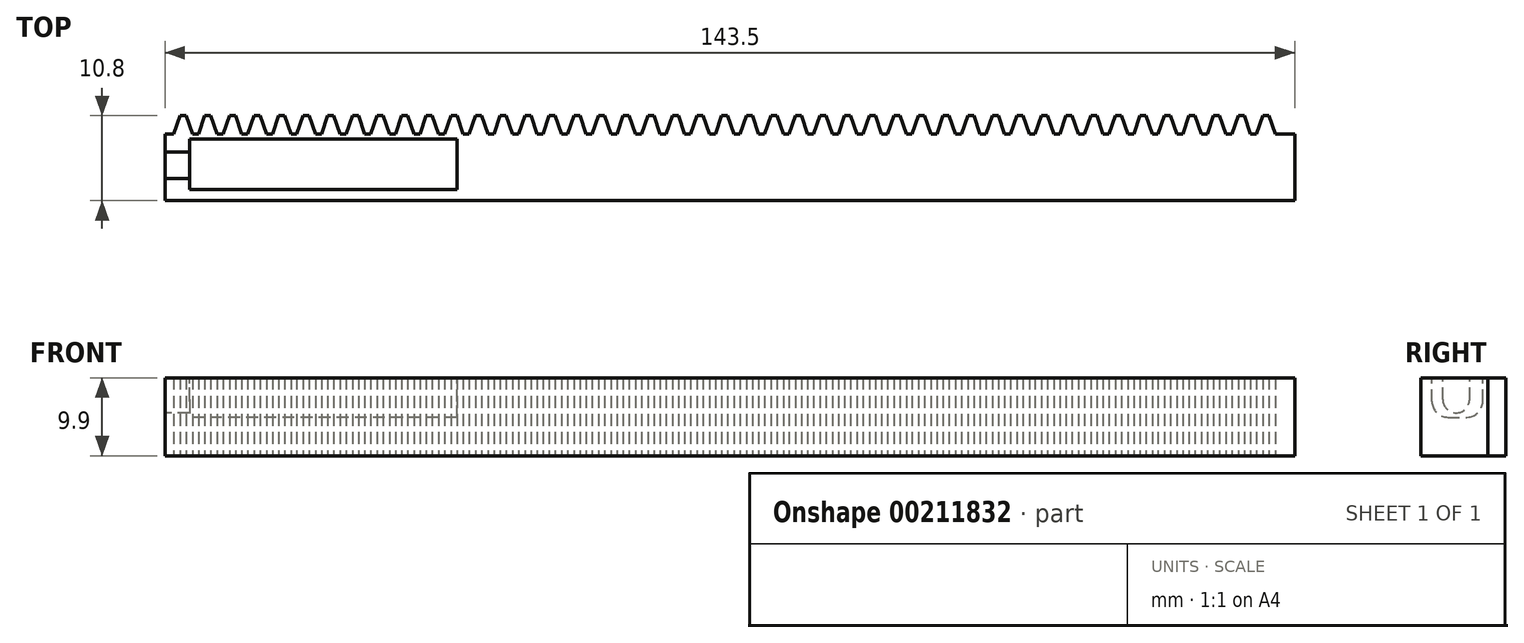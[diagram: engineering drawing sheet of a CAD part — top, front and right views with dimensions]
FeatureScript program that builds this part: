
annotation { "Feature Type Name" : "Feature", "Feature Type Description" : "" }
export const myFeature = defineFeature(function(context is Context, id is Id, definition is map)
    precondition{}
    {
        {
            var Q0;
            Q0=qCreatedBy(makeId("Top.planeOp"),FACE);
            var sketch = newSketch(context, id + "F0", { "sketchPlane" : qUnion([Q0])});
            skLineSegment(sketch, "E0.bottom", {"start": v(0, 0) * mm, "end": v(143.5, 0) * mm});
            skLineSegment(sketch, "E0.top", {"start": v(0, -8.5) * mm, "end": v(143.5, -8.5) * mm});
            skLineSegment(sketch, "E0.left", {"start": v(0, 0) * mm, "end": v(0, -8.5) * mm});
            skLineSegment(sketch, "E0.right", {"start": v(143.5, 0) * mm, "end": v(143.5, -8.5) * mm});
            skLineSegment(sketch, "E1", {"start": v(1.9, 2.3) * mm, "end": v(2.67, 2.3) * mm});
            skLineSegment(sketch, "E2", {"start": v(2.67, 2.3) * mm, "end": v(3.47, 0) * mm});
            skLineSegment(sketch, "E3", {"start": v(3.47, 0) * mm, "end": v(4.23, 0) * mm});
            skLineSegment(sketch, "E4", {"start": v(4.23, 0) * mm, "end": v(5.04, 2.3) * mm});
            skLineSegment(sketch, "E5", {"start": v(5.04, 2.3) * mm, "end": v(5.8, 2.3) * mm});
            skLineSegment(sketch, "E6", {"start": v(5.8, 2.3) * mm, "end": v(6.6, 0) * mm});
            skLineSegment(sketch, "E7", {"start": v(6.6, 0) * mm, "end": v(7.36, 0) * mm});
            skLineSegment(sketch, "E8", {"start": v(7.36, 0) * mm, "end": v(8.17, 2.3) * mm});
            skLineSegment(sketch, "E9", {"start": v(8.17, 2.3) * mm, "end": v(8.93, 2.3) * mm});
            skLineSegment(sketch, "E10", {"start": v(8.93, 2.3) * mm, "end": v(9.73, 0) * mm});
            skLineSegment(sketch, "E11", {"start": v(9.73, 0) * mm, "end": v(16.36, 0) * mm});
            skLineSegment(sketch, "E12", {"start": v(1.9, 2.3) * mm, "end": v(1.1, 0) * mm});
            skLineSegment(sketch, "E13", {"start": v(2.28, 2.3) * mm, "end": v(2.28, 0) * mm});
            skLineSegment(sketch, "E14", {"start": v(9.73, 0) * mm, "end": v(10.5, 0) * mm});
            skLineSegment(sketch, "E15", {"start": v(10.5, 0) * mm, "end": v(11.3, 2.3) * mm});
            skLineSegment(sketch, "E16", {"start": v(11.3, 2.3) * mm, "end": v(12.06, 2.3) * mm});
            skLineSegment(sketch, "E17", {"start": v(12.06, 2.3) * mm, "end": v(12.86, 0) * mm});
            skLineSegment(sketch, "E18", {"start": v(12.86, 0) * mm, "end": v(13.62, 0) * mm});
            skLineSegment(sketch, "E19", {"start": v(13.62, 0) * mm, "end": v(14.43, 2.3) * mm});
            skLineSegment(sketch, "E20", {"start": v(14.43, 2.3) * mm, "end": v(15.19, 2.3) * mm});
            skLineSegment(sketch, "E21", {"start": v(15.19, 2.3) * mm, "end": v(16, 0) * mm});
            skLineSegment(sketch, "E22", {"start": v(13.62, 0) * mm, "end": v(12.86, 0) * mm});
            skLineSegment(sketch, "E23", {"start": v(10.5, 0) * mm, "end": v(9.73, 0) * mm});
            skPoint(sketch, "E24", {"position": v(0.73, 0) * mm});
            skPoint(sketch, "E25", {"position": v(32, 0) * mm});
            skPoint(sketch, "E26", {"position": v(47.62, 0) * mm});
            skPoint(sketch, "E27", {"position": v(63.25, 0) * mm});
            skPoint(sketch, "E28", {"position": v(78.88, 0) * mm});
            skPoint(sketch, "E29", {"position": v(94.51, 0) * mm});
            skPoint(sketch, "E30", {"position": v(110.14, 0) * mm});
            skPoint(sketch, "E31", {"position": v(125.76, 0) * mm});
            skPoint(sketch, "E32", {"position": v(141.4, 0) * mm});
            skLineSegment(sketch, "E33", {"start": v(16.36, 0) * mm, "end": v(16.36, -2.94) * mm});
            skLineSegment(sketch, "E34", {"start": v(32, 0) * mm, "end": v(32, -2.44) * mm});
            skLineSegment(sketch, "E35", {"start": v(47.62, 0) * mm, "end": v(47.62, -3.03) * mm});
            skLineSegment(sketch, "E36", {"start": v(63.25, 0) * mm, "end": v(63.25, -3.22) * mm});
            skLineSegment(sketch, "E37", {"start": v(78.88, 0) * mm, "end": v(78.88, -3.55) * mm});
            skLineSegment(sketch, "E38", {"start": v(94.51, 0) * mm, "end": v(94.51, -3.55) * mm});
            skLineSegment(sketch, "E39", {"start": v(110.14, 0) * mm, "end": v(110.14, -2.9) * mm});
            skLineSegment(sketch, "E40", {"start": v(125.76, 0) * mm, "end": v(125.76, -2.77) * mm});
            skLineSegment(sketch, "E41.MirrorCS", {"start": v(22.23, 0) * mm, "end": v(23, 0) * mm});
            skLineSegment(sketch, "E42.MirrorCS", {"start": v(26.12, 0) * mm, "end": v(25.36, 0) * mm});
            skLineSegment(sketch, "E43.MirrorCS", {"start": v(23, 0) * mm, "end": v(16.36, 0) * mm});
            skLineSegment(sketch, "E44.MirrorCS", {"start": v(23, 0) * mm, "end": v(22.23, 0) * mm});
            skLineSegment(sketch, "E45.MirrorCS", {"start": v(30.82, 2.3) * mm, "end": v(30.06, 2.3) * mm});
            skLineSegment(sketch, "E46.MirrorCS", {"start": v(19.86, 0) * mm, "end": v(19.1, 0) * mm});
            skLineSegment(sketch, "E47.MirrorCS", {"start": v(21.43, 2.3) * mm, "end": v(20.67, 2.3) * mm});
            skLineSegment(sketch, "E48.MirrorCS", {"start": v(22.23, 0) * mm, "end": v(21.43, 2.3) * mm});
            skLineSegment(sketch, "E49.MirrorCS", {"start": v(32.72, 0) * mm, "end": v(-110.78, 0) * mm});
            skLineSegment(sketch, "E50.MirrorCS", {"start": v(26.93, 2.3) * mm, "end": v(26.12, 0) * mm});
            skLineSegment(sketch, "E51.MirrorCS", {"start": v(23.8, 2.3) * mm, "end": v(23, 0) * mm});
            skLineSegment(sketch, "E52.MirrorCS", {"start": v(19.1, 0) * mm, "end": v(19.86, 0) * mm});
            skLineSegment(sketch, "E53.MirrorCS", {"start": v(27.69, 2.3) * mm, "end": v(26.93, 2.3) * mm});
            skLineSegment(sketch, "E54.MirrorCS", {"start": v(24.56, 2.3) * mm, "end": v(23.8, 2.3) * mm});
            skLineSegment(sketch, "E55.MirrorCS", {"start": v(18.3, 2.3) * mm, "end": v(17.53, 2.3) * mm});
            skLineSegment(sketch, "E56.MirrorCS", {"start": v(19.1, 0) * mm, "end": v(18.3, 2.3) * mm});
            skLineSegment(sketch, "E57.MirrorCS", {"start": v(20.67, 2.3) * mm, "end": v(19.86, 0) * mm});
            skLineSegment(sketch, "E58.MirrorCS", {"start": v(25.36, 0) * mm, "end": v(24.56, 2.3) * mm});
            skLineSegment(sketch, "E59.MirrorCS", {"start": v(28.5, 0) * mm, "end": v(27.69, 2.3) * mm});
            skLineSegment(sketch, "E60.MirrorCS", {"start": v(30.82, 2.3) * mm, "end": v(31.62, 0) * mm});
            skLineSegment(sketch, "E61.MirrorCS", {"start": v(30.06, 2.3) * mm, "end": v(29.25, 0) * mm});
            skLineSegment(sketch, "E62.MirrorCS", {"start": v(29.25, 0) * mm, "end": v(28.5, 0) * mm});
            skLineSegment(sketch, "E63.MirrorCS", {"start": v(17.53, 2.3) * mm, "end": v(16.73, 0) * mm});
            skLineSegment(sketch, "E64.MirrorCS", {"start": v(30.44, 2.3) * mm, "end": v(30.44, 0) * mm});
            skLineSegment(sketch, "E65.MirrorCS", {"start": v(53.5, 0) * mm, "end": v(54.25, 0) * mm});
            skLineSegment(sketch, "E66.MirrorCS", {"start": v(41.75, 0) * mm, "end": v(41, 0) * mm});
            skLineSegment(sketch, "E67.MirrorCS", {"start": v(41, 0) * mm, "end": v(41.75, 0) * mm});
            skLineSegment(sketch, "E68.MirrorCS", {"start": v(54.25, 0) * mm, "end": v(53.5, 0) * mm});
            skLineSegment(sketch, "E69.MirrorCS", {"start": v(51.12, 0) * mm, "end": v(50.36, 0) * mm});
            skLineSegment(sketch, "E70.MirrorCS", {"start": v(44.88, 0) * mm, "end": v(44.12, 0) * mm});
            skLineSegment(sketch, "E71.MirrorCS", {"start": v(50.36, 0) * mm, "end": v(51.12, 0) * mm});
            skLineSegment(sketch, "E72.MirrorCS", {"start": v(44.12, 0) * mm, "end": v(44.88, 0) * mm});
            skLineSegment(sketch, "E73.MirrorCS", {"start": v(47.62, 0) * mm, "end": v(47.62, -2.94) * mm});
            skLineSegment(sketch, "E74.MirrorCS", {"start": v(45.69, 2.3) * mm, "end": v(46.45, 2.3) * mm});
            skLineSegment(sketch, "E75.MirrorCS", {"start": v(39.43, 2.3) * mm, "end": v(40.19, 2.3) * mm});
            skLineSegment(sketch, "E76.MirrorCS", {"start": v(33.17, 2.3) * mm, "end": v(33.93, 2.3) * mm});
            skLineSegment(sketch, "E77.MirrorCS", {"start": v(36.3, 2.3) * mm, "end": v(37.06, 2.3) * mm});
            skLineSegment(sketch, "E78.MirrorCS", {"start": v(49.55, 2.3) * mm, "end": v(48.8, 2.3) * mm});
            skLineSegment(sketch, "E79.MirrorCS", {"start": v(55.82, 2.3) * mm, "end": v(55.06, 2.3) * mm});
            skLineSegment(sketch, "E80.MirrorCS", {"start": v(57.38, 0) * mm, "end": v(56.62, 0) * mm});
            skLineSegment(sketch, "E81.MirrorCS", {"start": v(58.95, 2.3) * mm, "end": v(58.19, 2.3) * mm});
            skLineSegment(sketch, "E82.MirrorCS", {"start": v(60.51, 0) * mm, "end": v(59.75, 0) * mm});
            skLineSegment(sketch, "E83.MirrorCS", {"start": v(42.56, 2.3) * mm, "end": v(43.32, 2.3) * mm});
            skLineSegment(sketch, "E84.MirrorCS", {"start": v(37.86, 0) * mm, "end": v(38.62, 0) * mm});
            skLineSegment(sketch, "E85.MirrorCS", {"start": v(62.08, 2.3) * mm, "end": v(61.32, 2.3) * mm});
            skLineSegment(sketch, "E86.MirrorCS", {"start": v(52.69, 2.3) * mm, "end": v(51.93, 2.3) * mm});
            skLineSegment(sketch, "E87.MirrorCS", {"start": v(34.73, 0) * mm, "end": v(35.5, 0) * mm});
            skLineSegment(sketch, "E88.MirrorCS", {"start": v(54.25, 0) * mm, "end": v(47.62, 0) * mm});
            skLineSegment(sketch, "E89.MirrorCS", {"start": v(41, 0) * mm, "end": v(47.62, 0) * mm});
            skLineSegment(sketch, "E90.MirrorCS", {"start": v(31.26, 0) * mm, "end": v(174.76, 0) * mm});
            skLineSegment(sketch, "E91.MirrorCS", {"start": v(53.5, 0) * mm, "end": v(52.69, 2.3) * mm});
            skLineSegment(sketch, "E92.MirrorCS", {"start": v(48.8, 2.3) * mm, "end": v(47.99, 0) * mm});
            skLineSegment(sketch, "E93.MirrorCS", {"start": v(33.93, 2.3) * mm, "end": v(34.73, 0) * mm});
            skLineSegment(sketch, "E94.MirrorCS", {"start": v(61.7, 2.3) * mm, "end": v(61.7, 0) * mm});
            skLineSegment(sketch, "E95.MirrorCS", {"start": v(33.17, 2.3) * mm, "end": v(32.36, 0) * mm});
            skLineSegment(sketch, "E96.MirrorCS", {"start": v(56.62, 0) * mm, "end": v(55.82, 2.3) * mm});
            skLineSegment(sketch, "E97.MirrorCS", {"start": v(58.19, 2.3) * mm, "end": v(57.38, 0) * mm});
            skLineSegment(sketch, "E98.MirrorCS", {"start": v(59.75, 0) * mm, "end": v(58.95, 2.3) * mm});
            skLineSegment(sketch, "E99.MirrorCS", {"start": v(33.55, 2.3) * mm, "end": v(33.55, 0) * mm});
            skLineSegment(sketch, "E100.MirrorCS", {"start": v(40.19, 2.3) * mm, "end": v(41, 0) * mm});
            skLineSegment(sketch, "E101.MirrorCS", {"start": v(38.62, 0) * mm, "end": v(39.43, 2.3) * mm});
            skLineSegment(sketch, "E102.MirrorCS", {"start": v(37.06, 2.3) * mm, "end": v(37.86, 0) * mm});
            skLineSegment(sketch, "E103.MirrorCS", {"start": v(43.32, 2.3) * mm, "end": v(44.12, 0) * mm});
            skLineSegment(sketch, "E104.MirrorCS", {"start": v(51.93, 2.3) * mm, "end": v(51.12, 0) * mm});
            skLineSegment(sketch, "E105.MirrorCS", {"start": v(62.08, 2.3) * mm, "end": v(62.88, 0) * mm});
            skLineSegment(sketch, "E106.MirrorCS", {"start": v(41.75, 0) * mm, "end": v(42.56, 2.3) * mm});
            skLineSegment(sketch, "E107.MirrorCS", {"start": v(46.45, 2.3) * mm, "end": v(47.25, 0) * mm});
            skLineSegment(sketch, "E108.MirrorCS", {"start": v(61.32, 2.3) * mm, "end": v(60.51, 0) * mm});
            skLineSegment(sketch, "E109.MirrorCS", {"start": v(35.5, 0) * mm, "end": v(36.3, 2.3) * mm});
            skLineSegment(sketch, "E110.MirrorCS", {"start": v(55.06, 2.3) * mm, "end": v(54.25, 0) * mm});
            skLineSegment(sketch, "E111.MirrorCS", {"start": v(44.88, 0) * mm, "end": v(45.69, 2.3) * mm});
            skLineSegment(sketch, "E112.MirrorCS", {"start": v(50.36, 0) * mm, "end": v(49.55, 2.3) * mm});
            skLineSegment(sketch, "E113.MirrorCS", {"start": v(63.98, 0) * mm, "end": v(-79.52, 0) * mm});
            skLineSegment(sketch, "E114.MirrorCS", {"start": v(84.75, 0) * mm, "end": v(85.51, 0) * mm});
            skLineSegment(sketch, "E115.MirrorCS", {"start": v(116.01, 0) * mm, "end": v(116.77, 0) * mm});
            skLineSegment(sketch, "E116.MirrorCS", {"start": v(73.01, 0) * mm, "end": v(72.25, 0) * mm});
            skLineSegment(sketch, "E117.MirrorCS", {"start": v(104.27, 0) * mm, "end": v(103.51, 0) * mm});
            skLineSegment(sketch, "E118.MirrorCS", {"start": v(78.88, 0) * mm, "end": v(78.88, -3.03) * mm});
            skLineSegment(sketch, "E119.MirrorCS", {"start": v(85.51, 0) * mm, "end": v(84.75, 0) * mm});
            skLineSegment(sketch, "E120.MirrorCS", {"start": v(72.25, 0) * mm, "end": v(73.01, 0) * mm});
            skLineSegment(sketch, "E121.MirrorCS", {"start": v(78.88, 0) * mm, "end": v(78.88, -2.94) * mm});
            skLineSegment(sketch, "E122.MirrorCS", {"start": v(103.51, 0) * mm, "end": v(104.27, 0) * mm});
            skLineSegment(sketch, "E123.MirrorCS", {"start": v(116.77, 0) * mm, "end": v(116.01, 0) * mm});
            skLineSegment(sketch, "E124.MirrorCS", {"start": v(94.51, 0) * mm, "end": v(94.51, -2.44) * mm});
            skLineSegment(sketch, "E125.MirrorCS", {"start": v(75.38, 0) * mm, "end": v(76.14, 0) * mm});
            skLineSegment(sketch, "E126.MirrorCS", {"start": v(81.62, 0) * mm, "end": v(82.38, 0) * mm});
            skLineSegment(sketch, "E127.MirrorCS", {"start": v(107.4, 0) * mm, "end": v(106.64, 0) * mm});
            skLineSegment(sketch, "E128.MirrorCS", {"start": v(113.64, 0) * mm, "end": v(112.88, 0) * mm});
            skLineSegment(sketch, "E129.MirrorCS", {"start": v(112.88, 0) * mm, "end": v(113.64, 0) * mm});
            skLineSegment(sketch, "E130.MirrorCS", {"start": v(106.64, 0) * mm, "end": v(107.4, 0) * mm});
            skLineSegment(sketch, "E131.MirrorCS", {"start": v(123.03, 0) * mm, "end": v(122.27, 0) * mm});
            skLineSegment(sketch, "E132.MirrorCS", {"start": v(76.14, 0) * mm, "end": v(75.38, 0) * mm});
            skLineSegment(sketch, "E133.MirrorCS", {"start": v(110.14, 0) * mm, "end": v(110.14, -2.94) * mm});
            skLineSegment(sketch, "E134.MirrorCS", {"start": v(82.38, 0) * mm, "end": v(81.62, 0) * mm});
            skLineSegment(sketch, "E135.MirrorCS", {"start": v(108.2, 2.3) * mm, "end": v(108.97, 2.3) * mm});
            skLineSegment(sketch, "E136.MirrorCS", {"start": v(88.64, 0) * mm, "end": v(87.88, 0) * mm});
            skLineSegment(sketch, "E137.MirrorCS", {"start": v(87.08, 2.3) * mm, "end": v(86.32, 2.3) * mm});
            skLineSegment(sketch, "E138.MirrorCS", {"start": v(101.95, 2.3) * mm, "end": v(102.7, 2.3) * mm});
            skLineSegment(sketch, "E139.MirrorCS", {"start": v(83.95, 2.3) * mm, "end": v(83.19, 2.3) * mm});
            skLineSegment(sketch, "E140.MirrorCS", {"start": v(80.81, 2.3) * mm, "end": v(80.05, 2.3) * mm});
            skLineSegment(sketch, "E141.MirrorCS", {"start": v(95.69, 2.3) * mm, "end": v(96.45, 2.3) * mm});
            skLineSegment(sketch, "E142.MirrorCS", {"start": v(98.82, 2.3) * mm, "end": v(99.58, 2.3) * mm});
            skLineSegment(sketch, "E143.MirrorCS", {"start": v(66, 0) * mm, "end": v(66.75, 0) * mm});
            skLineSegment(sketch, "E144.MirrorCS", {"start": v(112.07, 2.3) * mm, "end": v(111.31, 2.3) * mm});
            skLineSegment(sketch, "E145.MirrorCS", {"start": v(118.34, 2.3) * mm, "end": v(117.58, 2.3) * mm});
            skLineSegment(sketch, "E146.MirrorCS", {"start": v(119.9, 0) * mm, "end": v(119.14, 0) * mm});
            skLineSegment(sketch, "E147.MirrorCS", {"start": v(121.47, 2.3) * mm, "end": v(120.7, 2.3) * mm});
            skLineSegment(sketch, "E148.MirrorCS", {"start": v(124.6, 2.3) * mm, "end": v(123.84, 2.3) * mm});
            skLineSegment(sketch, "E149.MirrorCS", {"start": v(97.25, 0) * mm, "end": v(98.01, 0) * mm});
            skLineSegment(sketch, "E150.MirrorCS", {"start": v(105.08, 2.3) * mm, "end": v(105.84, 2.3) * mm});
            skLineSegment(sketch, "E151.MirrorCS", {"start": v(93.34, 2.3) * mm, "end": v(92.58, 2.3) * mm});
            skLineSegment(sketch, "E152.MirrorCS", {"start": v(115.2, 2.3) * mm, "end": v(114.45, 2.3) * mm});
            skLineSegment(sketch, "E153.MirrorCS", {"start": v(64.43, 2.3) * mm, "end": v(65.19, 2.3) * mm});
            skLineSegment(sketch, "E154.MirrorCS", {"start": v(90.2, 2.3) * mm, "end": v(89.45, 2.3) * mm});
            skLineSegment(sketch, "E155.MirrorCS", {"start": v(70.69, 2.3) * mm, "end": v(71.45, 2.3) * mm});
            skLineSegment(sketch, "E156.MirrorCS", {"start": v(73.82, 2.3) * mm, "end": v(74.58, 2.3) * mm});
            skLineSegment(sketch, "E157.MirrorCS", {"start": v(69.12, 0) * mm, "end": v(69.88, 0) * mm});
            skLineSegment(sketch, "E158.MirrorCS", {"start": v(91.77, 0) * mm, "end": v(91.01, 0) * mm});
            skLineSegment(sketch, "E159.MirrorCS", {"start": v(93.78, 0) * mm, "end": v(237.28, 0) * mm});
            skLineSegment(sketch, "E160.MirrorCS", {"start": v(76.95, 2.3) * mm, "end": v(77.7, 2.3) * mm});
            skLineSegment(sketch, "E161.MirrorCS", {"start": v(67.56, 2.3) * mm, "end": v(68.32, 2.3) * mm});
            skLineSegment(sketch, "E162.MirrorCS", {"start": v(72.25, 0) * mm, "end": v(78.88, 0) * mm});
            skLineSegment(sketch, "E163.MirrorCS", {"start": v(100.38, 0) * mm, "end": v(101.14, 0) * mm});
            skLineSegment(sketch, "E164.MirrorCS", {"start": v(103.51, 0) * mm, "end": v(110.14, 0) * mm});
            skPoint(sketch, "E165.MirrorP", {"position": v(125.77, 0) * mm});
            skLineSegment(sketch, "E166.MirrorCS", {"start": v(85.51, 0) * mm, "end": v(78.88, 0) * mm});
            skLineSegment(sketch, "E167.MirrorCS", {"start": v(122.27, 0) * mm, "end": v(121.47, 2.3) * mm});
            skLineSegment(sketch, "E168.MirrorCS", {"start": v(123.84, 2.3) * mm, "end": v(123.03, 0) * mm});
            skLineSegment(sketch, "E169.MirrorCS", {"start": v(116.77, 0) * mm, "end": v(110.14, 0) * mm});
            skLineSegment(sketch, "E170.MirrorCS", {"start": v(62.52, 0) * mm, "end": v(206.02, 0) * mm});
            skLineSegment(sketch, "E171.MirrorCS", {"start": v(86.32, 2.3) * mm, "end": v(85.51, 0) * mm});
            skLineSegment(sketch, "E172.MirrorCS", {"start": v(116.01, 0) * mm, "end": v(115.2, 2.3) * mm});
            skLineSegment(sketch, "E173.MirrorCS", {"start": v(73.01, 0) * mm, "end": v(73.82, 2.3) * mm});
            skLineSegment(sketch, "E174.MirrorCS", {"start": v(80.05, 2.3) * mm, "end": v(79.25, 0) * mm});
            skLineSegment(sketch, "E175.MirrorCS", {"start": v(92.96, 2.3) * mm, "end": v(92.96, 0) * mm});
            skLineSegment(sketch, "E176.MirrorCS", {"start": v(95.24, 0) * mm, "end": v(-48.26, 0) * mm});
            skLineSegment(sketch, "E177.MirrorCS", {"start": v(84.75, 0) * mm, "end": v(83.95, 2.3) * mm});
            skLineSegment(sketch, "E178.MirrorCS", {"start": v(111.31, 2.3) * mm, "end": v(110.5, 0) * mm});
            skLineSegment(sketch, "E179.MirrorCS", {"start": v(96.45, 2.3) * mm, "end": v(97.25, 0) * mm});
            skLineSegment(sketch, "E180.MirrorCS", {"start": v(124.22, 2.3) * mm, "end": v(124.22, 0) * mm});
            skLineSegment(sketch, "E181.MirrorCS", {"start": v(64.43, 2.3) * mm, "end": v(63.62, 0) * mm});
            skLineSegment(sketch, "E182.MirrorCS", {"start": v(95.69, 2.3) * mm, "end": v(94.88, 0) * mm});
            skLineSegment(sketch, "E183.MirrorCS", {"start": v(66.75, 0) * mm, "end": v(67.56, 2.3) * mm});
            skLineSegment(sketch, "E184.MirrorCS", {"start": v(119.14, 0) * mm, "end": v(118.34, 2.3) * mm});
            skLineSegment(sketch, "E185.MirrorCS", {"start": v(120.7, 2.3) * mm, "end": v(119.9, 0) * mm});
            skLineSegment(sketch, "E186.MirrorCS", {"start": v(126.5, 0) * mm, "end": v(-17, 0) * mm});
            skLineSegment(sketch, "E187.MirrorCS", {"start": v(65.19, 2.3) * mm, "end": v(66, 0) * mm});
            skLineSegment(sketch, "E188.MirrorCS", {"start": v(77.7, 2.3) * mm, "end": v(78.51, 0) * mm});
            skLineSegment(sketch, "E189.MirrorCS", {"start": v(107.4, 0) * mm, "end": v(108.2, 2.3) * mm});
            skLineSegment(sketch, "E190.MirrorCS", {"start": v(87.88, 0) * mm, "end": v(87.08, 2.3) * mm});
            skLineSegment(sketch, "E191.MirrorCS", {"start": v(108.97, 2.3) * mm, "end": v(109.77, 0) * mm});
            skLineSegment(sketch, "E192.MirrorCS", {"start": v(104.27, 0) * mm, "end": v(105.08, 2.3) * mm});
            skLineSegment(sketch, "E193.MirrorCS", {"start": v(91.01, 0) * mm, "end": v(90.2, 2.3) * mm});
            skLineSegment(sketch, "E194.MirrorCS", {"start": v(92.58, 2.3) * mm, "end": v(91.77, 0) * mm});
            skLineSegment(sketch, "E195.MirrorCS", {"start": v(114.45, 2.3) * mm, "end": v(113.64, 0) * mm});
            skLineSegment(sketch, "E196.MirrorCS", {"start": v(124.6, 2.3) * mm, "end": v(125.4, 0) * mm});
            skLineSegment(sketch, "E197.MirrorCS", {"start": v(99.58, 2.3) * mm, "end": v(100.38, 0) * mm});
            skLineSegment(sketch, "E198.MirrorCS", {"start": v(68.32, 2.3) * mm, "end": v(69.12, 0) * mm});
            skLineSegment(sketch, "E199.MirrorCS", {"start": v(117.58, 2.3) * mm, "end": v(116.77, 0) * mm});
            skLineSegment(sketch, "E200.MirrorCS", {"start": v(105.84, 2.3) * mm, "end": v(106.64, 0) * mm});
            skLineSegment(sketch, "E201.MirrorCS", {"start": v(98.01, 0) * mm, "end": v(98.82, 2.3) * mm});
            skLineSegment(sketch, "E202.MirrorCS", {"start": v(96.07, 2.3) * mm, "end": v(96.07, 0) * mm});
            skLineSegment(sketch, "E203.MirrorCS", {"start": v(81.62, 0) * mm, "end": v(80.81, 2.3) * mm});
            skLineSegment(sketch, "E204.MirrorCS", {"start": v(89.45, 2.3) * mm, "end": v(88.64, 0) * mm});
            skLineSegment(sketch, "E205.MirrorCS", {"start": v(64.8, 2.3) * mm, "end": v(64.8, 0) * mm});
            skLineSegment(sketch, "E206.MirrorCS", {"start": v(74.58, 2.3) * mm, "end": v(75.38, 0) * mm});
            skLineSegment(sketch, "E207.MirrorCS", {"start": v(93.34, 2.3) * mm, "end": v(94.14, 0) * mm});
            skLineSegment(sketch, "E208.MirrorCS", {"start": v(71.45, 2.3) * mm, "end": v(72.25, 0) * mm});
            skLineSegment(sketch, "E209.MirrorCS", {"start": v(69.88, 0) * mm, "end": v(70.69, 2.3) * mm});
            skLineSegment(sketch, "E210.MirrorCS", {"start": v(83.19, 2.3) * mm, "end": v(82.38, 0) * mm});
            skLineSegment(sketch, "E211.MirrorCS", {"start": v(76.14, 0) * mm, "end": v(76.95, 2.3) * mm});
            skLineSegment(sketch, "E212.MirrorCS", {"start": v(102.7, 2.3) * mm, "end": v(103.51, 0) * mm});
            skLineSegment(sketch, "E213.MirrorCS", {"start": v(101.14, 0) * mm, "end": v(101.95, 2.3) * mm});
            skLineSegment(sketch, "E214.MirrorCS", {"start": v(112.88, 0) * mm, "end": v(112.07, 2.3) * mm});
            skLineSegment(sketch, "E215.MirrorCS", {"start": v(134.75, 0) * mm, "end": v(135.51, 0) * mm});
            skLineSegment(sketch, "E216.MirrorCS", {"start": v(135.51, 0) * mm, "end": v(134.75, 0) * mm});
            skLineSegment(sketch, "E217.MirrorCS", {"start": v(220.26, 0) * mm, "end": v(76.76, 0) * mm});
            skLineSegment(sketch, "E218.MirrorCS", {"start": v(138.64, 0) * mm, "end": v(137.88, 0) * mm});
            skLineSegment(sketch, "E219.MirrorCS", {"start": v(134.75, 0) * mm, "end": v(141.38, 0) * mm});
            skLineSegment(sketch, "E220.MirrorCS", {"start": v(137.88, 0) * mm, "end": v(138.64, 0) * mm});
            skLineSegment(sketch, "E221.MirrorCS", {"start": v(125.02, 0) * mm, "end": v(268.52, 0) * mm});
            skLineSegment(sketch, "E222.MirrorCS", {"start": v(126.93, 2.3) * mm, "end": v(127.69, 2.3) * mm});
            skLineSegment(sketch, "E223.MirrorCS", {"start": v(139.45, 2.3) * mm, "end": v(140.2, 2.3) * mm});
            skLineSegment(sketch, "E224.MirrorCS", {"start": v(133.19, 2.3) * mm, "end": v(133.95, 2.3) * mm});
            skLineSegment(sketch, "E225.MirrorCS", {"start": v(131.62, 0) * mm, "end": v(132.38, 0) * mm});
            skLineSegment(sketch, "E226.MirrorCS", {"start": v(189, 0) * mm, "end": v(45.5, 0) * mm});
            skLineSegment(sketch, "E227.MirrorCS", {"start": v(128.5, 0) * mm, "end": v(129.25, 0) * mm});
            skLineSegment(sketch, "E228.MirrorCS", {"start": v(130.06, 2.3) * mm, "end": v(130.82, 2.3) * mm});
            skLineSegment(sketch, "E229.MirrorCS", {"start": v(136.32, 2.3) * mm, "end": v(137.08, 2.3) * mm});
            skLineSegment(sketch, "E230.MirrorCS", {"start": v(251.52, 0) * mm, "end": v(108.02, 0) * mm});
            skLineSegment(sketch, "E231.MirrorCS", {"start": v(157.74, 0) * mm, "end": v(14.24, 0) * mm});
            skPoint(sketch, "E232.MirrorP", {"position": v(125.75, 0) * mm});
            skLineSegment(sketch, "E233.MirrorCS", {"start": v(135.51, 0) * mm, "end": v(136.32, 2.3) * mm});
            skLineSegment(sketch, "E234.MirrorCS", {"start": v(129.25, 0) * mm, "end": v(130.06, 2.3) * mm});
            skLineSegment(sketch, "E235.MirrorCS", {"start": v(133.95, 2.3) * mm, "end": v(134.75, 0) * mm});
            skLineSegment(sketch, "E236.MirrorCS", {"start": v(140.2, 2.3) * mm, "end": v(141.01, 0) * mm});
            skLineSegment(sketch, "E237.MirrorCS", {"start": v(132.38, 0) * mm, "end": v(133.19, 2.3) * mm});
            skLineSegment(sketch, "E238.MirrorCS", {"start": v(127.69, 2.3) * mm, "end": v(128.5, 0) * mm});
            skLineSegment(sketch, "E239.MirrorCS", {"start": v(137.08, 2.3) * mm, "end": v(137.88, 0) * mm});
            skLineSegment(sketch, "E240.MirrorCS", {"start": v(138.64, 0) * mm, "end": v(139.45, 2.3) * mm});
            skLineSegment(sketch, "E241.MirrorCS", {"start": v(130.82, 2.3) * mm, "end": v(131.62, 0) * mm});
            skLineSegment(sketch, "E242.MirrorCS", {"start": v(126.93, 2.3) * mm, "end": v(126.12, 0) * mm});
            skLineSegment(sketch, "E243.MirrorCS", {"start": v(127.3, 2.3) * mm, "end": v(127.3, 0) * mm});
            skPoint(sketch, "E244.MirrorP", {"position": v(141.38, 0) * mm});
            skSolve(sketch);
        }
        {
            var Q0;
            Q0 = qSketchRegion(id + "F0", true);
            extrude(context, id + "F1", {"entities" : qUnion([Q0]), "depth" : 9.9 * mm});
        }
        {
            var Q0;
            Q0=makeQuery(id+"F1.opExtrude","SWEPT_FACE",FACE,{"disambiguationData":[OSD([sQuery(id+"F0.wireOp",EDGE,"E0.left")])]});
            var sketch = newSketch(context, id + "F2", { "sketchPlane" : qUnion([Q0])});
            skLineSegment(sketch, "E245.bottom", {"start": v(0, 9.9) * mm, "end": v(4, 9.9) * mm});
            skLineSegment(sketch, "E245.top", {"start": v(0, 5.45) * mm, "end": v(4, 5.45) * mm});
            skLineSegment(sketch, "E245.left", {"start": v(0, 9.9) * mm, "end": v(0, 5.45) * mm});
            skLineSegment(sketch, "E245.right", {"start": v(4, 9.9) * mm, "end": v(4, 5.45) * mm});
            skCircle(sketch, "E246", {"center": v(4, 7.15) * mm, "radius": 1.7 * mm});
            skLineSegment(sketch, "E247", {"start": v(2.3, 7.15) * mm, "end": v(2.3, 9.9) * mm});
            skLineSegment(sketch, "E248", {"start": v(5.7, 7.15) * mm, "end": v(5.7, 9.9) * mm});
            skSolve(sketch);
        }
        {
            var Q0;
            {var subQ3=sQuery(id+"F2.wireOp",EDGE,"E247");Q0=makeQuery(id+"F2.imprint","IMPRINT",FACE,{"disambiguationData":[TD([[makeQuery(id+"F2.imprint","IMPRINT",EDGE,{"derivedFrom":subQ3}),-1.0]])]});}
            var Q1;
            {var subQ0=sQuery(id+"F2.wireOp",EDGE,"E246");var subQ4=makeQuery(id+"F2.imprint","INTERSECT",VERTEX,{"derivedFrom":[subQ0,sQuery(id+"F2.wireOp",EDGE,"E248")]});Q1=makeQuery(id+"F2.imprint","IMPRINT",FACE,{"disambiguationData":[TD([[makeQuery(id+"F2.imprint","IMPRINT",EDGE,{"disambiguationData":[TD([[subQ4,-1.0]])],"derivedFrom":subQ0}),1.0]])]});}
            var Q2;
            {var subQ0=sQuery(id+"F2.wireOp",EDGE,"E246");var subQ4=makeQuery(id+"F2.imprint","INTERSECT",VERTEX,{"derivedFrom":[subQ0,sQuery(id+"F2.wireOp",EDGE,"E247")]});Q2=makeQuery(id+"F2.imprint","IMPRINT",FACE,{"disambiguationData":[TD([[makeQuery(id+"F2.imprint","IMPRINT",EDGE,{"disambiguationData":[TD([[subQ4,1.0]])],"derivedFrom":subQ0}),1.0]])]});}
            var Q3;
            {var subQ5=sQuery(id+"F2.wireOp",EDGE,"E248");Q3=makeQuery(id+"F2.imprint","IMPRINT",FACE,{"disambiguationData":[TD([[makeQuery(id+"F2.imprint","IMPRINT",EDGE,{"derivedFrom":subQ5}),1.0]])]});}
            extrude(context, id + "F3", {"entities" : qUnion([Q0, Q1, Q2, Q3]), "operationType" : NewBodyOperationType.REMOVE, "oppositeDirection" : true, "depth" : 3.1 * mm});
        }
        {
            var Q0;
            Q0=makeQuery(id+"F1.opExtrude","CAP_FACE",FACE,{"disambiguationData":[OSD([sQuery(id+"F0.wireOp",EDGE,"E0.top"),sQuery(id+"F0.wireOp",EDGE,"E0.left"),sQuery(id+"F0.wireOp",EDGE,"E0.right"),sQuery(id+"F0.wireOp",EDGE,"E1"),sQuery(id+"F0.wireOp",EDGE,"E2"),sQuery(id+"F0.wireOp",EDGE,"E4"),sQuery(id+"F0.wireOp",EDGE,"E5"),sQuery(id+"F0.wireOp",EDGE,"E6"),sQuery(id+"F0.wireOp",EDGE,"E8"),sQuery(id+"F0.wireOp",EDGE,"E9"),sQuery(id+"F0.wireOp",EDGE,"E10"),sQuery(id+"F0.wireOp",EDGE,"E12"),sQuery(id+"F0.wireOp",EDGE,"E15"),sQuery(id+"F0.wireOp",EDGE,"E16"),sQuery(id+"F0.wireOp",EDGE,"E17"),sQuery(id+"F0.wireOp",EDGE,"E19"),sQuery(id+"F0.wireOp",EDGE,"E20"),sQuery(id+"F0.wireOp",EDGE,"E21"),sQuery(id+"F0.wireOp",EDGE,"E45.MirrorCS"),sQuery(id+"F0.wireOp",EDGE,"E47.MirrorCS"),sQuery(id+"F0.wireOp",EDGE,"E48.MirrorCS"),sQuery(id+"F0.wireOp",EDGE,"E50.MirrorCS"),sQuery(id+"F0.wireOp",EDGE,"E51.MirrorCS"),sQuery(id+"F0.wireOp",EDGE,"E53.MirrorCS"),sQuery(id+"F0.wireOp",EDGE,"E54.MirrorCS"),sQuery(id+"F0.wireOp",EDGE,"E55.MirrorCS"),sQuery(id+"F0.wireOp",EDGE,"E56.MirrorCS"),sQuery(id+"F0.wireOp",EDGE,"E57.MirrorCS"),sQuery(id+"F0.wireOp",EDGE,"E58.MirrorCS"),sQuery(id+"F0.wireOp",EDGE,"E59.MirrorCS"),sQuery(id+"F0.wireOp",EDGE,"E60.MirrorCS"),sQuery(id+"F0.wireOp",EDGE,"E61.MirrorCS"),sQuery(id+"F0.wireOp",EDGE,"E63.MirrorCS"),sQuery(id+"F0.wireOp",EDGE,"E74.MirrorCS"),sQuery(id+"F0.wireOp",EDGE,"E75.MirrorCS"),sQuery(id+"F0.wireOp",EDGE,"E76.MirrorCS"),sQuery(id+"F0.wireOp",EDGE,"E77.MirrorCS"),sQuery(id+"F0.wireOp",EDGE,"E78.MirrorCS"),sQuery(id+"F0.wireOp",EDGE,"E79.MirrorCS"),sQuery(id+"F0.wireOp",EDGE,"E81.MirrorCS"),sQuery(id+"F0.wireOp",EDGE,"E83.MirrorCS"),sQuery(id+"F0.wireOp",EDGE,"E85.MirrorCS"),sQuery(id+"F0.wireOp",EDGE,"E86.MirrorCS"),sQuery(id+"F0.wireOp",EDGE,"E91.MirrorCS"),sQuery(id+"F0.wireOp",EDGE,"E92.MirrorCS"),sQuery(id+"F0.wireOp",EDGE,"E93.MirrorCS"),sQuery(id+"F0.wireOp",EDGE,"E95.MirrorCS"),sQuery(id+"F0.wireOp",EDGE,"E96.MirrorCS"),sQuery(id+"F0.wireOp",EDGE,"E97.MirrorCS"),sQuery(id+"F0.wireOp",EDGE,"E98.MirrorCS"),sQuery(id+"F0.wireOp",EDGE,"E100.MirrorCS"),sQuery(id+"F0.wireOp",EDGE,"E101.MirrorCS"),sQuery(id+"F0.wireOp",EDGE,"E102.MirrorCS"),sQuery(id+"F0.wireOp",EDGE,"E103.MirrorCS"),sQuery(id+"F0.wireOp",EDGE,"E104.MirrorCS"),sQuery(id+"F0.wireOp",EDGE,"E105.MirrorCS"),sQuery(id+"F0.wireOp",EDGE,"E106.MirrorCS"),sQuery(id+"F0.wireOp",EDGE,"E107.MirrorCS"),sQuery(id+"F0.wireOp",EDGE,"E108.MirrorCS"),sQuery(id+"F0.wireOp",EDGE,"E109.MirrorCS"),sQuery(id+"F0.wireOp",EDGE,"E110.MirrorCS"),sQuery(id+"F0.wireOp",EDGE,"E111.MirrorCS"),sQuery(id+"F0.wireOp",EDGE,"E112.MirrorCS"),sQuery(id+"F0.wireOp",EDGE,"E135.MirrorCS"),sQuery(id+"F0.wireOp",EDGE,"E137.MirrorCS"),sQuery(id+"F0.wireOp",EDGE,"E138.MirrorCS"),sQuery(id+"F0.wireOp",EDGE,"E139.MirrorCS"),sQuery(id+"F0.wireOp",EDGE,"E140.MirrorCS"),sQuery(id+"F0.wireOp",EDGE,"E141.MirrorCS"),sQuery(id+"F0.wireOp",EDGE,"E142.MirrorCS"),sQuery(id+"F0.wireOp",EDGE,"E144.MirrorCS"),sQuery(id+"F0.wireOp",EDGE,"E145.MirrorCS"),sQuery(id+"F0.wireOp",EDGE,"E147.MirrorCS"),sQuery(id+"F0.wireOp",EDGE,"E148.MirrorCS"),sQuery(id+"F0.wireOp",EDGE,"E150.MirrorCS"),sQuery(id+"F0.wireOp",EDGE,"E151.MirrorCS"),sQuery(id+"F0.wireOp",EDGE,"E152.MirrorCS"),sQuery(id+"F0.wireOp",EDGE,"E153.MirrorCS"),sQuery(id+"F0.wireOp",EDGE,"E154.MirrorCS"),sQuery(id+"F0.wireOp",EDGE,"E155.MirrorCS"),sQuery(id+"F0.wireOp",EDGE,"E156.MirrorCS"),sQuery(id+"F0.wireOp",EDGE,"E160.MirrorCS"),sQuery(id+"F0.wireOp",EDGE,"E161.MirrorCS"),sQuery(id+"F0.wireOp",EDGE,"E167.MirrorCS"),sQuery(id+"F0.wireOp",EDGE,"E168.MirrorCS"),sQuery(id+"F0.wireOp",EDGE,"E171.MirrorCS"),sQuery(id+"F0.wireOp",EDGE,"E172.MirrorCS"),sQuery(id+"F0.wireOp",EDGE,"E173.MirrorCS"),sQuery(id+"F0.wireOp",EDGE,"E174.MirrorCS"),sQuery(id+"F0.wireOp",EDGE,"E177.MirrorCS"),sQuery(id+"F0.wireOp",EDGE,"E178.MirrorCS"),sQuery(id+"F0.wireOp",EDGE,"E179.MirrorCS"),sQuery(id+"F0.wireOp",EDGE,"E181.MirrorCS"),sQuery(id+"F0.wireOp",EDGE,"E182.MirrorCS"),sQuery(id+"F0.wireOp",EDGE,"E183.MirrorCS"),sQuery(id+"F0.wireOp",EDGE,"E184.MirrorCS"),sQuery(id+"F0.wireOp",EDGE,"E185.MirrorCS"),sQuery(id+"F0.wireOp",EDGE,"E186.MirrorCS"),sQuery(id+"F0.wireOp",EDGE,"E187.MirrorCS"),sQuery(id+"F0.wireOp",EDGE,"E188.MirrorCS"),sQuery(id+"F0.wireOp",EDGE,"E189.MirrorCS"),sQuery(id+"F0.wireOp",EDGE,"E190.MirrorCS"),sQuery(id+"F0.wireOp",EDGE,"E191.MirrorCS"),sQuery(id+"F0.wireOp",EDGE,"E192.MirrorCS"),sQuery(id+"F0.wireOp",EDGE,"E193.MirrorCS"),sQuery(id+"F0.wireOp",EDGE,"E194.MirrorCS"),sQuery(id+"F0.wireOp",EDGE,"E195.MirrorCS"),sQuery(id+"F0.wireOp",EDGE,"E196.MirrorCS"),sQuery(id+"F0.wireOp",EDGE,"E197.MirrorCS"),sQuery(id+"F0.wireOp",EDGE,"E198.MirrorCS"),sQuery(id+"F0.wireOp",EDGE,"E199.MirrorCS"),sQuery(id+"F0.wireOp",EDGE,"E200.MirrorCS"),sQuery(id+"F0.wireOp",EDGE,"E201.MirrorCS"),sQuery(id+"F0.wireOp",EDGE,"E203.MirrorCS"),sQuery(id+"F0.wireOp",EDGE,"E204.MirrorCS"),sQuery(id+"F0.wireOp",EDGE,"E206.MirrorCS"),sQuery(id+"F0.wireOp",EDGE,"E207.MirrorCS"),sQuery(id+"F0.wireOp",EDGE,"E208.MirrorCS"),sQuery(id+"F0.wireOp",EDGE,"E209.MirrorCS"),sQuery(id+"F0.wireOp",EDGE,"E210.MirrorCS"),sQuery(id+"F0.wireOp",EDGE,"E211.MirrorCS"),sQuery(id+"F0.wireOp",EDGE,"E212.MirrorCS"),sQuery(id+"F0.wireOp",EDGE,"E213.MirrorCS"),sQuery(id+"F0.wireOp",EDGE,"E214.MirrorCS"),sQuery(id+"F0.wireOp",EDGE,"E222.MirrorCS"),sQuery(id+"F0.wireOp",EDGE,"E223.MirrorCS"),sQuery(id+"F0.wireOp",EDGE,"E224.MirrorCS"),sQuery(id+"F0.wireOp",EDGE,"E228.MirrorCS"),sQuery(id+"F0.wireOp",EDGE,"E229.MirrorCS"),sQuery(id+"F0.wireOp",EDGE,"E231.MirrorCS"),sQuery(id+"F0.wireOp",EDGE,"E233.MirrorCS"),sQuery(id+"F0.wireOp",EDGE,"E234.MirrorCS"),sQuery(id+"F0.wireOp",EDGE,"E235.MirrorCS"),sQuery(id+"F0.wireOp",EDGE,"E236.MirrorCS"),sQuery(id+"F0.wireOp",EDGE,"E237.MirrorCS"),sQuery(id+"F0.wireOp",EDGE,"E238.MirrorCS"),sQuery(id+"F0.wireOp",EDGE,"E239.MirrorCS"),sQuery(id+"F0.wireOp",EDGE,"E240.MirrorCS"),sQuery(id+"F0.wireOp",EDGE,"E241.MirrorCS"),sQuery(id+"F0.wireOp",EDGE,"E242.MirrorCS")])],"isStart":false});
            var sketch = newSketch(context, id + "F4", { "sketchPlane" : qUnion([Q0])});
            skLineSegment(sketch, "E249", {"start": v(3.1, -2.3) * mm, "end": v(3.1, -0.63) * mm});
            skLineSegment(sketch, "E250", {"start": v(3.1, -0.63) * mm, "end": v(37.1, -0.63) * mm});
            skLineSegment(sketch, "E251", {"start": v(37.1, -0.63) * mm, "end": v(37.1, -7.08) * mm});
            skLineSegment(sketch, "E252", {"start": v(37.1, -7.08) * mm, "end": v(3.1, -7.08) * mm});
            skLineSegment(sketch, "E253", {"start": v(3.1, -7.08) * mm, "end": v(3.1, -2.3) * mm});
            skSolve(sketch);
        }
        {
            var Q0;
            Q0 = qSketchRegion(id + "F4", true);
            extrude(context, id + "F5", {"entities" : qUnion([Q0]), "operationType" : NewBodyOperationType.REMOVE, "oppositeDirection" : true, "depth" : 5 * mm});
        }
        {
            var Q0;
            Q0=makeQuery(id+"F5.boolean.opBoolean","COPY",EDGE,{"derivedFrom":makeQuery(id+"F5.opExtrude","CAP_EDGE",EDGE,{"disambiguationData":[OSD([sQuery(id+"F4.wireOp",EDGE,"E250")])],"isStart":false})});
            var Q1;
            Q1=makeQuery(id+"F5.boolean.opBoolean","COPY",EDGE,{"derivedFrom":makeQuery(id+"F5.opExtrude","CAP_EDGE",EDGE,{"disambiguationData":[OSD([sQuery(id+"F4.wireOp",EDGE,"E252")])],"isStart":false})});
            fillet(context, id + "F6", {"entities" : qUnion([Q0, Q1]), "radius" : 2 * mm, "tangentPropagation" : true, "allowEdgeOverflow" : false});
        }
    });
